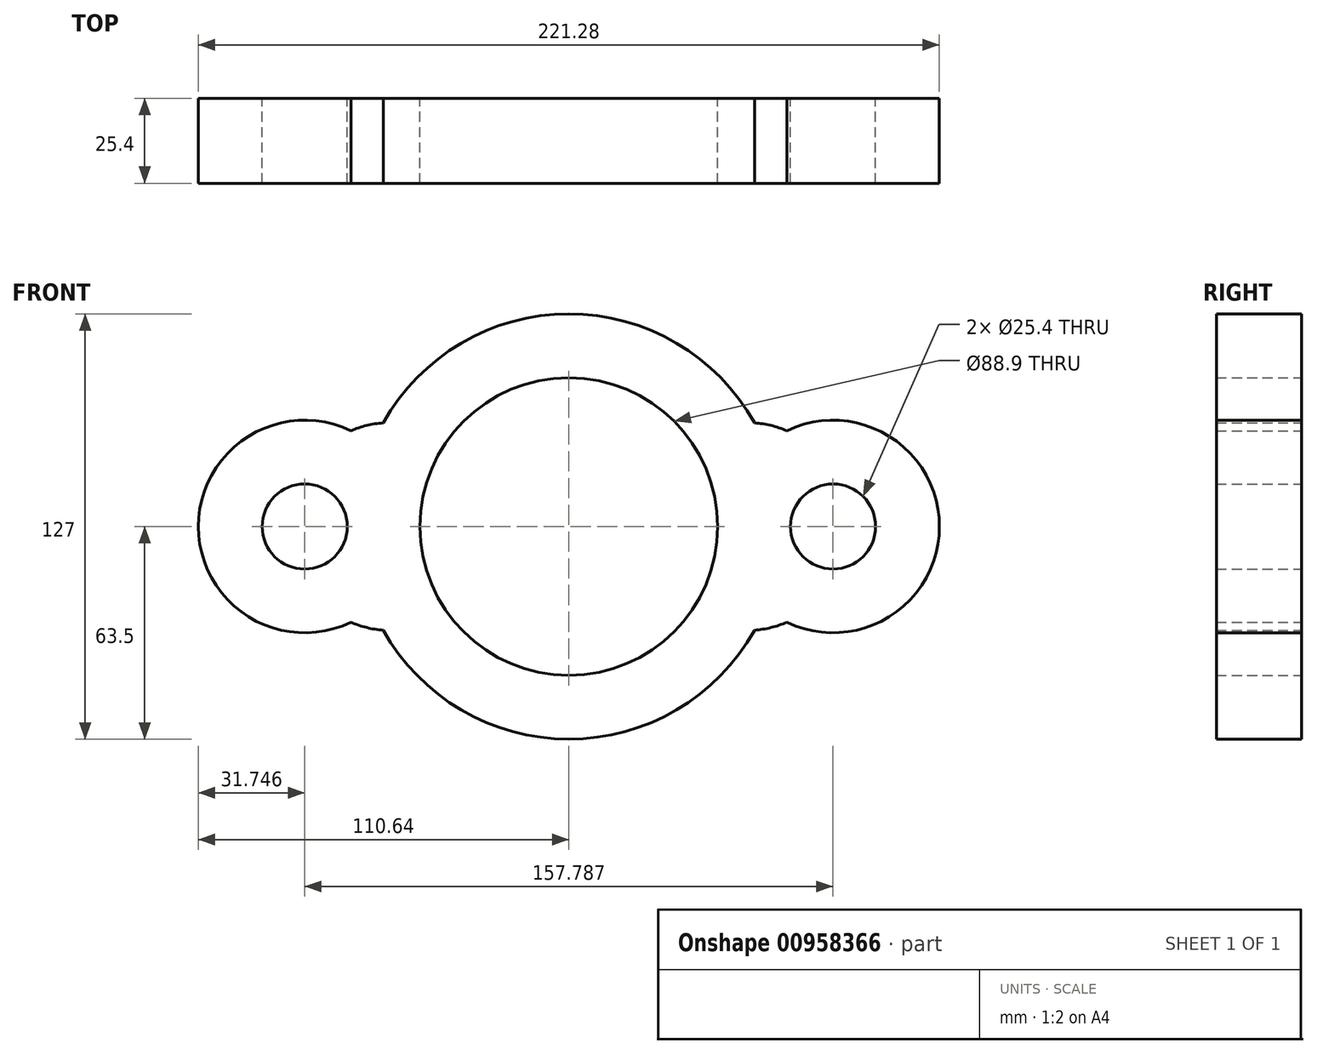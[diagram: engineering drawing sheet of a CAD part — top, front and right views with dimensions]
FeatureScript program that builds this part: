
annotation { "Feature Type Name" : "Feature", "Feature Type Description" : "" }
export const myFeature = defineFeature(function(context is Context, id is Id, definition is map)
    precondition{}
    {
        {
            var Q0;
            Q0=qCreatedBy(makeId("Front.planeOp"),FACE);
            var sketch = newSketch(context, id + "F0", { "sketchPlane" : qUnion([Q0])});
            skCircle(sketch, "E0", {"center": v(0, 0) * mm, "radius": 44.45 * mm});
            skArc(sketch, "E1", {"start": v(55.45, 30.94) * mm, "mid": v(-63.5, 0) * mm, "end": v(55.45, -30.94) * mm});
            skLineSegment(sketch, "E2", {"start": v(0, 0) * mm, "end": v(78.9, 0) * mm});
            skLineSegment(sketch, "E3.MirrorCS", {"start": v(0, 0) * mm, "end": v(-78.9, 0) * mm});
            skCircle(sketch, "E4", {"center": v(78.9, 0) * mm, "radius": 12.7 * mm});
            skArc(sketch, "E5", {"start": v(65.1, -28.6) * mm, "mid": v(110.64, 0) * mm, "end": v(65.1, 28.6) * mm});
            skArc(sketch, "E6", {"start": v(65.1, 28.6) * mm, "mid": v(60.37, 30.17) * mm, "end": v(55.45, 30.94) * mm});
            skArc(sketch, "E7.MirrorCS", {"start": v(65.1, -28.6) * mm, "mid": v(60.37, -30.17) * mm, "end": v(55.45, -30.94) * mm});
            skArc(sketch, "E8.MirrorCS", {"start": v(-65.1, 28.6) * mm, "mid": v(-60.37, 30.17) * mm, "end": v(-55.45, 30.94) * mm});
            skArc(sketch, "E9.MirrorCS", {"start": v(-65.1, -28.6) * mm, "mid": v(-110.64, 0) * mm, "end": v(-65.1, 28.6) * mm});
            skArc(sketch, "E10.MirrorCS", {"start": v(-65.1, -28.6) * mm, "mid": v(-60.37, -30.17) * mm, "end": v(-55.45, -30.94) * mm});
            skCircle(sketch, "E11.MirrorC", {"center": v(-78.9, 0) * mm, "radius": 12.7 * mm});
            skSolve(sketch);
        }
        {
            var Q0;
            Q0 = qSketchRegion(id + "F0", true);
            extrude(context, id + "F1", {"entities" : qUnion([Q0]), "depth" : 25.4 * mm, "offsetDistance" : 25.4 * mm});
        }
    });
